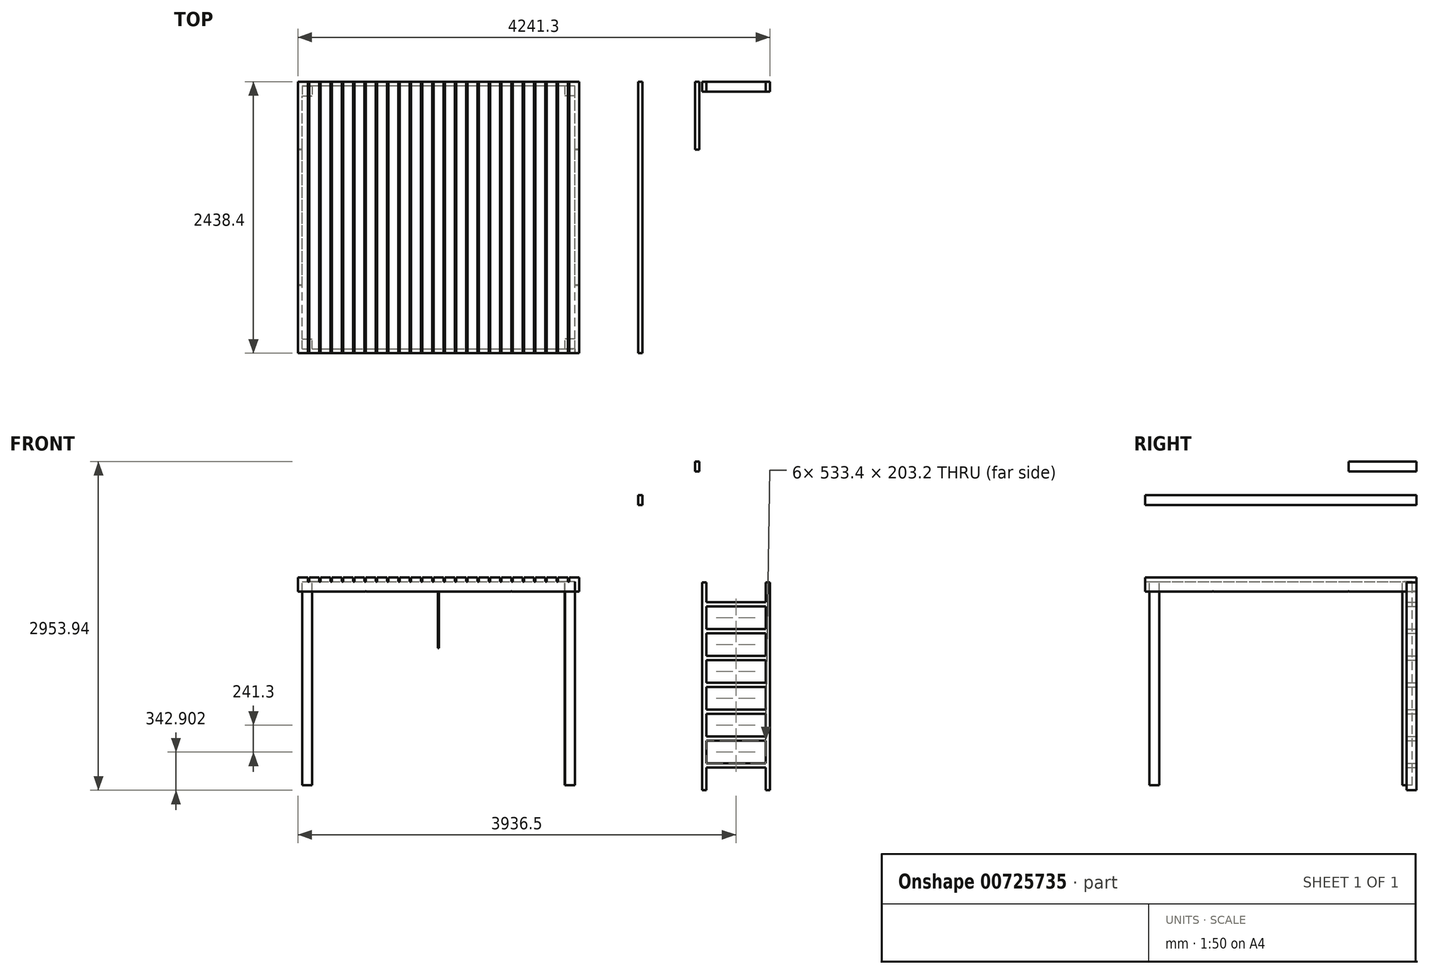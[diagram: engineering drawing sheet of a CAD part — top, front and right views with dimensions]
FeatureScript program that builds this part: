
annotation { "Feature Type Name" : "Feature", "Feature Type Description" : "" }
export const myFeature = defineFeature(function(context is Context, id is Id, definition is map)
    precondition{}
    {
        {
            var Q0;
            Q0=qCreatedBy(makeId("Front.planeOp"),FACE);
            var sketch = newSketch(context, id + "F0", { "sketchPlane" : qUnion([Q0])});
            skLineSegment(sketch, "E0.bottom", {"start": v(1225.55, 515.62) * mm, "end": v(-1225.55, 515.62) * mm});
            skLineSegment(sketch, "E0.top", {"start": v(1225.55, 604.52) * mm, "end": v(-1225.55, 604.52) * mm});
            skLineSegment(sketch, "E0.left", {"start": v(1225.55, 515.62) * mm, "end": v(1225.55, 604.52) * mm});
            skLineSegment(sketch, "E0.right", {"start": v(-1225.55, 515.62) * mm, "end": v(-1225.55, 604.52) * mm});
            skPoint(sketch, "E0.middle", {"position": v(0, 560.07) * mm});
            skLineSegment(sketch, "E1.bottom", {"start": v(1225.55, 515.62) * mm, "end": v(1263.65, 515.62) * mm});
            skLineSegment(sketch, "E1.top", {"start": v(1225.55, 604.52) * mm, "end": v(1263.65, 604.52) * mm});
            skLineSegment(sketch, "E1.right", {"start": v(1263.65, 515.62) * mm, "end": v(1263.65, 604.52) * mm});
            skLineSegment(sketch, "E2.bottom", {"start": v(-1225.55, 515.62) * mm, "end": v(-1263.65, 515.62) * mm});
            skLineSegment(sketch, "E2.top", {"start": v(-1225.55, 604.52) * mm, "end": v(-1263.65, 604.52) * mm});
            skLineSegment(sketch, "E2.right", {"start": v(-1263.65, 515.62) * mm, "end": v(-1263.65, 604.52) * mm});
            skLineSegment(sketch, "E3.bottom", {"start": v(-1263.65, 604.52) * mm, "end": v(-1174.75, 604.52) * mm});
            skLineSegment(sketch, "E3.top", {"start": v(-1263.65, 642.62) * mm, "end": v(-1174.75, 642.62) * mm});
            skLineSegment(sketch, "E3.left", {"start": v(-1263.65, 604.52) * mm, "end": v(-1263.65, 642.62) * mm});
            skLineSegment(sketch, "E3.right", {"start": v(-1174.75, 604.52) * mm, "end": v(-1174.75, 642.62) * mm});
            skLineSegment(sketch, "E4.bottom", {"start": v(-1162.05, 604.52) * mm, "end": v(-1073.15, 604.52) * mm});
            skLineSegment(sketch, "E4.top", {"start": v(-1162.05, 642.62) * mm, "end": v(-1073.15, 642.62) * mm});
            skLineSegment(sketch, "E4.left", {"start": v(-1162.05, 604.52) * mm, "end": v(-1162.05, 642.62) * mm});
            skLineSegment(sketch, "E4.right", {"start": v(-1073.15, 604.52) * mm, "end": v(-1073.15, 642.62) * mm});
            skLineSegment(sketch, "E5.bottom", {"start": v(-1060.45, 604.52) * mm, "end": v(-971.55, 604.52) * mm});
            skLineSegment(sketch, "E5.top", {"start": v(-1060.45, 642.62) * mm, "end": v(-971.55, 642.62) * mm});
            skLineSegment(sketch, "E5.left", {"start": v(-1060.45, 604.52) * mm, "end": v(-1060.45, 642.62) * mm});
            skLineSegment(sketch, "E5.right", {"start": v(-971.55, 604.52) * mm, "end": v(-971.55, 642.62) * mm});
            skLineSegment(sketch, "E6.bottom", {"start": v(-958.85, 604.52) * mm, "end": v(-869.95, 604.52) * mm});
            skLineSegment(sketch, "E6.top", {"start": v(-958.85, 642.62) * mm, "end": v(-869.95, 642.62) * mm});
            skLineSegment(sketch, "E6.left", {"start": v(-958.85, 604.52) * mm, "end": v(-958.85, 642.62) * mm});
            skLineSegment(sketch, "E6.right", {"start": v(-869.95, 604.52) * mm, "end": v(-869.95, 642.62) * mm});
            skLineSegment(sketch, "E7.bottom", {"start": v(-857.25, 604.52) * mm, "end": v(-768.35, 604.52) * mm});
            skLineSegment(sketch, "E7.top", {"start": v(-857.25, 642.62) * mm, "end": v(-768.35, 642.62) * mm});
            skLineSegment(sketch, "E7.left", {"start": v(-857.25, 604.52) * mm, "end": v(-857.25, 642.62) * mm});
            skLineSegment(sketch, "E7.right", {"start": v(-768.35, 604.52) * mm, "end": v(-768.35, 642.62) * mm});
            skLineSegment(sketch, "E8.bottom", {"start": v(-755.65, 604.52) * mm, "end": v(-666.75, 604.52) * mm});
            skLineSegment(sketch, "E8.top", {"start": v(-755.65, 642.62) * mm, "end": v(-666.75, 642.62) * mm});
            skLineSegment(sketch, "E8.left", {"start": v(-755.65, 604.52) * mm, "end": v(-755.65, 642.62) * mm});
            skLineSegment(sketch, "E8.right", {"start": v(-666.75, 604.52) * mm, "end": v(-666.75, 642.62) * mm});
            skLineSegment(sketch, "E9.bottom", {"start": v(-654.05, 604.52) * mm, "end": v(-565.15, 604.52) * mm});
            skLineSegment(sketch, "E9.top", {"start": v(-654.05, 642.62) * mm, "end": v(-565.15, 642.62) * mm});
            skLineSegment(sketch, "E9.left", {"start": v(-654.05, 604.52) * mm, "end": v(-654.05, 642.62) * mm});
            skLineSegment(sketch, "E9.right", {"start": v(-565.15, 604.52) * mm, "end": v(-565.15, 642.62) * mm});
            skLineSegment(sketch, "E10.bottom", {"start": v(-552.45, 604.52) * mm, "end": v(-463.55, 604.52) * mm});
            skLineSegment(sketch, "E10.top", {"start": v(-552.45, 642.62) * mm, "end": v(-463.55, 642.62) * mm});
            skLineSegment(sketch, "E10.left", {"start": v(-552.45, 604.52) * mm, "end": v(-552.45, 642.62) * mm});
            skLineSegment(sketch, "E10.right", {"start": v(-463.55, 604.52) * mm, "end": v(-463.55, 642.62) * mm});
            skLineSegment(sketch, "E11.bottom", {"start": v(-450.85, 604.52) * mm, "end": v(-361.95, 604.52) * mm});
            skLineSegment(sketch, "E11.top", {"start": v(-450.85, 642.62) * mm, "end": v(-361.95, 642.62) * mm});
            skLineSegment(sketch, "E11.left", {"start": v(-450.85, 604.52) * mm, "end": v(-450.85, 642.62) * mm});
            skLineSegment(sketch, "E11.right", {"start": v(-361.95, 604.52) * mm, "end": v(-361.95, 642.62) * mm});
            skLineSegment(sketch, "E12.bottom", {"start": v(-349.25, 604.52) * mm, "end": v(-260.35, 604.52) * mm});
            skLineSegment(sketch, "E12.top", {"start": v(-349.25, 642.62) * mm, "end": v(-260.35, 642.62) * mm});
            skLineSegment(sketch, "E12.left", {"start": v(-349.25, 604.52) * mm, "end": v(-349.25, 642.62) * mm});
            skLineSegment(sketch, "E12.right", {"start": v(-260.35, 604.52) * mm, "end": v(-260.35, 642.62) * mm});
            skLineSegment(sketch, "E13.bottom", {"start": v(-247.65, 604.52) * mm, "end": v(-158.75, 604.52) * mm});
            skLineSegment(sketch, "E13.top", {"start": v(-247.65, 642.62) * mm, "end": v(-158.75, 642.62) * mm});
            skLineSegment(sketch, "E13.left", {"start": v(-247.65, 604.52) * mm, "end": v(-247.65, 642.62) * mm});
            skLineSegment(sketch, "E13.right", {"start": v(-158.75, 604.52) * mm, "end": v(-158.75, 642.62) * mm});
            skLineSegment(sketch, "E14.bottom", {"start": v(-146.05, 604.52) * mm, "end": v(-57.15, 604.52) * mm});
            skLineSegment(sketch, "E14.top", {"start": v(-146.05, 642.62) * mm, "end": v(-57.15, 642.62) * mm});
            skLineSegment(sketch, "E14.left", {"start": v(-146.05, 604.52) * mm, "end": v(-146.05, 642.62) * mm});
            skLineSegment(sketch, "E14.right", {"start": v(-57.15, 604.52) * mm, "end": v(-57.15, 642.62) * mm});
            skLineSegment(sketch, "E15.MirrorCS", {"start": v(57.15, 604.52) * mm, "end": v(57.15, 642.62) * mm});
            skLineSegment(sketch, "E16.MirrorCS", {"start": v(146.05, 642.62) * mm, "end": v(57.15, 642.62) * mm});
            skLineSegment(sketch, "E17.MirrorCS", {"start": v(146.05, 604.52) * mm, "end": v(146.05, 642.62) * mm});
            skLineSegment(sketch, "E18.MirrorCS", {"start": v(158.75, 604.52) * mm, "end": v(158.75, 642.62) * mm});
            skLineSegment(sketch, "E19.MirrorCS", {"start": v(247.65, 642.62) * mm, "end": v(158.75, 642.62) * mm});
            skLineSegment(sketch, "E20.MirrorCS", {"start": v(247.65, 604.52) * mm, "end": v(247.65, 642.62) * mm});
            skLineSegment(sketch, "E21.MirrorCS", {"start": v(260.35, 604.52) * mm, "end": v(260.35, 642.62) * mm});
            skLineSegment(sketch, "E22.MirrorCS", {"start": v(349.25, 642.62) * mm, "end": v(260.35, 642.62) * mm});
            skLineSegment(sketch, "E23.MirrorCS", {"start": v(349.25, 604.52) * mm, "end": v(349.25, 642.62) * mm});
            skLineSegment(sketch, "E24.MirrorCS", {"start": v(361.95, 604.52) * mm, "end": v(361.95, 642.62) * mm});
            skLineSegment(sketch, "E25.MirrorCS", {"start": v(450.85, 642.62) * mm, "end": v(361.95, 642.62) * mm});
            skLineSegment(sketch, "E26.MirrorCS", {"start": v(450.85, 604.52) * mm, "end": v(450.85, 642.62) * mm});
            skLineSegment(sketch, "E27.MirrorCS", {"start": v(463.55, 604.52) * mm, "end": v(463.55, 642.62) * mm});
            skLineSegment(sketch, "E28.MirrorCS", {"start": v(552.45, 642.62) * mm, "end": v(463.55, 642.62) * mm});
            skLineSegment(sketch, "E29.MirrorCS", {"start": v(552.45, 604.52) * mm, "end": v(552.45, 642.62) * mm});
            skLineSegment(sketch, "E30.MirrorCS", {"start": v(565.15, 604.52) * mm, "end": v(565.15, 642.62) * mm});
            skLineSegment(sketch, "E31.MirrorCS", {"start": v(654.05, 642.62) * mm, "end": v(565.15, 642.62) * mm});
            skLineSegment(sketch, "E32.MirrorCS", {"start": v(654.05, 604.52) * mm, "end": v(654.05, 642.62) * mm});
            skLineSegment(sketch, "E33.MirrorCS", {"start": v(666.75, 604.52) * mm, "end": v(666.75, 642.62) * mm});
            skLineSegment(sketch, "E34.MirrorCS", {"start": v(755.65, 642.62) * mm, "end": v(666.75, 642.62) * mm});
            skLineSegment(sketch, "E35.MirrorCS", {"start": v(755.65, 604.52) * mm, "end": v(755.65, 642.62) * mm});
            skLineSegment(sketch, "E36.MirrorCS", {"start": v(768.35, 604.52) * mm, "end": v(768.35, 642.62) * mm});
            skLineSegment(sketch, "E37.MirrorCS", {"start": v(857.25, 642.62) * mm, "end": v(768.35, 642.62) * mm});
            skLineSegment(sketch, "E38.MirrorCS", {"start": v(857.25, 604.52) * mm, "end": v(857.25, 642.62) * mm});
            skLineSegment(sketch, "E39.MirrorCS", {"start": v(869.95, 604.52) * mm, "end": v(869.95, 642.62) * mm});
            skLineSegment(sketch, "E40.MirrorCS", {"start": v(958.85, 642.62) * mm, "end": v(869.95, 642.62) * mm});
            skLineSegment(sketch, "E41.MirrorCS", {"start": v(1263.65, 604.52) * mm, "end": v(1263.65, 642.62) * mm});
            skLineSegment(sketch, "E42.MirrorCS", {"start": v(1263.65, 642.62) * mm, "end": v(1174.75, 642.62) * mm});
            skLineSegment(sketch, "E43.MirrorCS", {"start": v(1174.75, 604.52) * mm, "end": v(1174.75, 642.62) * mm});
            skLineSegment(sketch, "E44.MirrorCS", {"start": v(1162.05, 604.52) * mm, "end": v(1162.05, 642.62) * mm});
            skLineSegment(sketch, "E45.MirrorCS", {"start": v(1162.05, 642.62) * mm, "end": v(1073.15, 642.62) * mm});
            skLineSegment(sketch, "E46.MirrorCS", {"start": v(1073.15, 604.52) * mm, "end": v(1073.15, 642.62) * mm});
            skLineSegment(sketch, "E47.MirrorCS", {"start": v(1060.45, 604.52) * mm, "end": v(1060.45, 642.62) * mm});
            skLineSegment(sketch, "E48.MirrorCS", {"start": v(1060.45, 642.62) * mm, "end": v(971.55, 642.62) * mm});
            skLineSegment(sketch, "E49.MirrorCS", {"start": v(971.55, 604.52) * mm, "end": v(971.55, 642.62) * mm});
            skLineSegment(sketch, "E50.MirrorCS", {"start": v(958.85, 604.52) * mm, "end": v(958.85, 642.62) * mm});
            skLineSegment(sketch, "E51.bottom", {"start": v(-44.45, 604.52) * mm, "end": v(44.45, 604.52) * mm});
            skLineSegment(sketch, "E51.top", {"start": v(-44.45, 642.62) * mm, "end": v(44.45, 642.62) * mm});
            skLineSegment(sketch, "E51.left", {"start": v(-44.45, 604.52) * mm, "end": v(-44.45, 642.62) * mm});
            skLineSegment(sketch, "E51.right", {"start": v(44.45, 604.52) * mm, "end": v(44.45, 642.62) * mm});
            skLineSegment(sketch, "E52.bottom", {"start": v(4.76, 7.62) * mm, "end": v(-4.76, 7.62) * mm});
            skLineSegment(sketch, "E52.top", {"start": v(4.76, 515.62) * mm, "end": v(-4.76, 515.62) * mm});
            skLineSegment(sketch, "E52.left", {"start": v(4.76, 7.62) * mm, "end": v(4.76, 515.62) * mm});
            skLineSegment(sketch, "E52.right", {"start": v(-4.76, 7.62) * mm, "end": v(-4.76, 515.62) * mm});
            skPoint(sketch, "E52.middle", {"position": v(0, 261.62) * mm});
            skLineSegment(sketch, "E53.bottom", {"start": v(2977.65, -1270.8) * mm, "end": v(2939.55, -1270.8) * mm});
            skLineSegment(sketch, "E53.top", {"start": v(2977.65, 596.1) * mm, "end": v(2939.55, 596.1) * mm});
            skLineSegment(sketch, "E53.left", {"start": v(2977.65, -1270.8) * mm, "end": v(2977.65, 596.1) * mm});
            skLineSegment(sketch, "E53.right", {"start": v(2368.05, -1270.8) * mm, "end": v(2368.05, 596.1) * mm});
            skPoint(sketch, "E53.middle", {"position": v(2672.85, -337.35) * mm});
            skLineSegment(sketch, "E54.left", {"start": v(2939.55, -1270.8) * mm, "end": v(2939.55, -1067.6) * mm});
            skLineSegment(sketch, "E54.right", {"start": v(2406.15, -1270.8) * mm, "end": v(2406.15, -1067.6) * mm});
            skLineSegment(sketch, "E55", {"start": v(2406.15, -1067.6) * mm, "end": v(2939.55, -1067.6) * mm});
            skLineSegment(sketch, "E56", {"start": v(2406.15, -1029.5) * mm, "end": v(2939.55, -1029.5) * mm});
            skLineSegment(sketch, "E57", {"start": v(2406.15, -826.3) * mm, "end": v(2939.55, -826.3) * mm});
            skPoint(sketch, "E58.orphan", {"position": v(2939.55, -337.35) * mm});
            skPoint(sketch, "E59.start.orphan", {"position": v(2406.15, -337.35) * mm});
            skLineSegment(sketch, "E60", {"start": v(2406.15, -788.2) * mm, "end": v(2939.55, -788.2) * mm});
            skLineSegment(sketch, "E61", {"start": v(2406.15, -585) * mm, "end": v(2939.55, -585) * mm});
            skLineSegment(sketch, "E62", {"start": v(2406.15, -546.9) * mm, "end": v(2939.55, -546.9) * mm});
            skLineSegment(sketch, "E63", {"start": v(2939.55, -343.7) * mm, "end": v(2406.15, -343.7) * mm});
            skLineSegment(sketch, "E64", {"start": v(2406.15, -305.6) * mm, "end": v(2939.55, -305.6) * mm});
            skLineSegment(sketch, "E65", {"start": v(2406.15, -102.4) * mm, "end": v(2939.55, -102.4) * mm});
            skLineSegment(sketch, "E66", {"start": v(2406.15, -64.3) * mm, "end": v(2939.55, -64.3) * mm});
            skLineSegment(sketch, "E67", {"start": v(2406.15, 138.9) * mm, "end": v(2939.55, 138.9) * mm});
            skLineSegment(sketch, "E68", {"start": v(2406.15, 177) * mm, "end": v(2939.55, 177) * mm});
            skLineSegment(sketch, "E69", {"start": v(2406.15, 380.2) * mm, "end": v(2939.55, 380.2) * mm});
            skLineSegment(sketch, "E70", {"start": v(2406.15, 418.3) * mm, "end": v(2939.55, 418.3) * mm});
            skLineSegment(sketch, "E71.trimOffspring", {"start": v(2406.15, 596.1) * mm, "end": v(2368.05, 596.1) * mm});
            skLineSegment(sketch, "E72.trimOffspring", {"start": v(2406.15, -1270.8) * mm, "end": v(2368.05, -1270.8) * mm});
            skLineSegment(sketch, "E73.trimOffspring", {"start": v(2939.55, -1029.5) * mm, "end": v(2939.55, -826.3) * mm});
            skLineSegment(sketch, "E74.trimOffspring", {"start": v(2939.55, -788.2) * mm, "end": v(2939.55, -585) * mm});
            skLineSegment(sketch, "E75.trimOffspring", {"start": v(2406.15, -1029.5) * mm, "end": v(2406.15, -826.3) * mm});
            skLineSegment(sketch, "E76.trimOffspring", {"start": v(2406.15, -788.2) * mm, "end": v(2406.15, -585) * mm});
            skLineSegment(sketch, "E77.trimOffspring", {"start": v(2406.15, -546.9) * mm, "end": v(2406.15, -343.7) * mm});
            skLineSegment(sketch, "E78.trimOffspring", {"start": v(2939.55, -546.9) * mm, "end": v(2939.55, -343.7) * mm});
            skLineSegment(sketch, "E79.trimOffspring", {"start": v(2939.55, -305.6) * mm, "end": v(2939.55, -102.4) * mm});
            skLineSegment(sketch, "E80.trimOffspring", {"start": v(2406.15, -305.6) * mm, "end": v(2406.15, -102.4) * mm});
            skLineSegment(sketch, "E81.trimOffspring", {"start": v(2406.15, -64.3) * mm, "end": v(2406.15, 138.9) * mm});
            skLineSegment(sketch, "E82.trimOffspring", {"start": v(2939.55, -64.3) * mm, "end": v(2939.55, 138.9) * mm});
            skLineSegment(sketch, "E83.trimOffspring", {"start": v(2406.15, 177) * mm, "end": v(2406.15, 380.2) * mm});
            skLineSegment(sketch, "E84.trimOffspring", {"start": v(2939.55, 177) * mm, "end": v(2939.55, 380.2) * mm});
            skLineSegment(sketch, "E85.trimOffspring", {"start": v(2406.15, 418.3) * mm, "end": v(2406.15, 596.1) * mm});
            skLineSegment(sketch, "E86.trimOffspring", {"start": v(2939.55, 418.3) * mm, "end": v(2939.55, 596.1) * mm});
            skLineSegment(sketch, "E87.bottom", {"start": v(1833.2, 1291.68) * mm, "end": v(1795.1, 1291.68) * mm});
            skLineSegment(sketch, "E87.top", {"start": v(1833.2, 1380.58) * mm, "end": v(1795.1, 1380.58) * mm});
            skLineSegment(sketch, "E87.left", {"start": v(1833.2, 1291.68) * mm, "end": v(1833.2, 1380.58) * mm});
            skLineSegment(sketch, "E87.right", {"start": v(1795.1, 1291.68) * mm, "end": v(1795.1, 1380.58) * mm});
            skPoint(sketch, "E87.middle", {"position": v(1814.15, 1336.13) * mm});
            skLineSegment(sketch, "E88.bottom", {"start": v(2342.66, 1594.24) * mm, "end": v(2304.56, 1594.24) * mm});
            skLineSegment(sketch, "E88.top", {"start": v(2342.66, 1683.14) * mm, "end": v(2304.56, 1683.14) * mm});
            skLineSegment(sketch, "E88.left", {"start": v(2342.66, 1594.24) * mm, "end": v(2342.66, 1683.14) * mm});
            skLineSegment(sketch, "E88.right", {"start": v(2304.56, 1594.24) * mm, "end": v(2304.56, 1683.14) * mm});
            skPoint(sketch, "E88.middle", {"position": v(2323.6, 1638.69) * mm});
            skPoint(sketch, "E89", {"position": v(530.16, 1053.68) * mm});
            skPoint(sketch, "E90", {"position": v(654.05, 515.62) * mm});
            skPoint(sketch, "E91", {"position": v(-654.05, 515.62) * mm});
            skSolve(sketch);
        }
        {
            var Q0;
            Q0=makeQuery(id+"F0.imprint","IMPRINT",FACE,{"disambiguationData":[TD([[makeQuery(id+"F0.imprint","IMPRINT",EDGE,{"derivedFrom":sQuery(id+"F0.wireOp",EDGE,"E0.left")}),-1.0]])]});
            var Q1;
            Q1=makeQuery(id+"F0.imprint","IMPRINT",FACE,{"disambiguationData":[TD([[makeQuery(id+"F0.imprint","IMPRINT",EDGE,{"derivedFrom":sQuery(id+"F0.wireOp",EDGE,"E0.right")}),1.0]])]});
            extrude(context, id + "F1", {"entities" : qUnion([Q0, Q1]), "depth" : 2438.4 * mm, "offsetDistance" : 25.4 * mm});
        }
        {
            var Q0;
            {var subQ37=sQuery(id+"F0.wireOp",EDGE,"E0.left");Q0=makeQuery(id+"F0.imprint","IMPRINT",FACE,{"disambiguationData":[TD([[makeQuery(id+"F0.imprint","IMPRINT",EDGE,{"derivedFrom":subQ37}),1.0]])]});}
            extrude(context, id + "F2", {"entities" : qUnion([Q0]), "operationType" : NewBodyOperationType.ADD, "depth" : 38.1 * mm, "offsetDistance" : 25.4 * mm});
        }
        {
            var Q0;
            Q0=makeQuery(id+"F2.boolean.opBoolean","MERGE",FACE,{"derivedFrom":[makeQuery(id+"F1.opExtrude","SWEPT_FACE",FACE,{"disambiguationData":[OSD([sQuery(id+"F0.wireOp",EDGE,"E1.top")])]}),makeQuery(id+"F1.opExtrude","SWEPT_FACE",FACE,{"disambiguationData":[OSD([sQuery(id+"F0.wireOp",EDGE,"E2.top")])]}),makeQuery(id+"F2.opExtrude","SWEPT_FACE",FACE,{"disambiguationData":[OSD([sQuery(id+"F0.wireOp",EDGE,"E0.top")])]})]});
            cPlane(context, id + "F3", {"entities" : qUnion([Q0]), "cplaneType" : CPlaneType.OFFSET, "offset" : 0 * mm, "width" : 152.4 * mm, "height" : 152.4 * mm});
        }
        {
            var Q0;
            Q0=qCreatedBy(id+"F3.planeOp",FACE);
            var sketch = newSketch(context, id + "F4", { "sketchPlane" : qUnion([Q0])});
            skLineSegment(sketch, "E92.bottom", {"start": v(-1225.55, -2400.3) * mm, "end": v(-1136.65, -2400.3) * mm});
            skLineSegment(sketch, "E92.top", {"start": v(-1225.55, -2311.4) * mm, "end": v(-1136.65, -2311.4) * mm});
            skLineSegment(sketch, "E92.left", {"start": v(-1225.55, -2400.3) * mm, "end": v(-1225.55, -2311.4) * mm});
            skLineSegment(sketch, "E92.right", {"start": v(-1136.65, -2400.3) * mm, "end": v(-1136.65, -2311.4) * mm});
            skLineSegment(sketch, "E93.bottom", {"start": v(1225.55, -2400.3) * mm, "end": v(1136.65, -2400.3) * mm});
            skLineSegment(sketch, "E93.top", {"start": v(1225.55, -2311.4) * mm, "end": v(1136.65, -2311.4) * mm});
            skLineSegment(sketch, "E93.left", {"start": v(1225.55, -2400.3) * mm, "end": v(1225.55, -2311.4) * mm});
            skLineSegment(sketch, "E93.right", {"start": v(1136.65, -2400.3) * mm, "end": v(1136.65, -2311.4) * mm});
            skLineSegment(sketch, "E94.bottom", {"start": v(-1226.27, -2400.3) * mm, "end": v(1224.83, -2400.3) * mm});
            skLineSegment(sketch, "E94.top", {"start": v(-1226.27, -2438.4) * mm, "end": v(1224.83, -2438.4) * mm});
            skLineSegment(sketch, "E94.left", {"start": v(-1226.27, -2400.3) * mm, "end": v(-1226.27, -2438.4) * mm});
            skLineSegment(sketch, "E94.right", {"start": v(1224.83, -2400.3) * mm, "end": v(1224.83, -2438.4) * mm});
            skLineSegment(sketch, "E95.bottom", {"start": v(-1226.02, -38.43) * mm, "end": v(-1137.12, -38.43) * mm});
            skLineSegment(sketch, "E95.top", {"start": v(-1226.02, -127.33) * mm, "end": v(-1137.12, -127.33) * mm});
            skLineSegment(sketch, "E95.left", {"start": v(-1226.02, -38.43) * mm, "end": v(-1226.02, -127.33) * mm});
            skLineSegment(sketch, "E95.right", {"start": v(-1137.12, -38.43) * mm, "end": v(-1137.12, -127.33) * mm});
            skLineSegment(sketch, "E96.bottom", {"start": v(1223.57, -39.1) * mm, "end": v(1134.67, -39.1) * mm});
            skLineSegment(sketch, "E96.top", {"start": v(1223.57, -128) * mm, "end": v(1134.67, -128) * mm});
            skLineSegment(sketch, "E96.left", {"start": v(1223.57, -39.1) * mm, "end": v(1223.57, -128) * mm});
            skLineSegment(sketch, "E96.right", {"start": v(1134.67, -39.1) * mm, "end": v(1134.67, -128) * mm});
            skSolve(sketch);
        }
        {
            var Q0;
            {var subQ1=sQuery(id+"F4.wireOp",EDGE,"E92.bottom");Q0=makeQuery(id+"F4.imprint","IMPRINT",FACE,{"disambiguationData":[TD([[makeQuery(id+"F4.imprint","IMPRINT",EDGE,{"derivedFrom":subQ1}),-1.0]])]});}
            extrude(context, id + "F5", {"entities" : qUnion([Q0]), "operationType" : NewBodyOperationType.ADD, "oppositeDirection" : true, "depth" : 88.9 * mm, "offsetDistance" : 25.4 * mm});
        }
        {
            var Q0;
            Q0=makeQuery(id+"F4.imprint","IMPRINT",FACE,{"disambiguationData":[TD([[makeQuery(id+"F4.imprint","IMPRINT",EDGE,{"derivedFrom":sQuery(id+"F4.wireOp",EDGE,"E92.bottom")}),1.0]])]});
            extrude(context, id + "F6", {"entities" : qUnion([Q0]), "operationType" : NewBodyOperationType.ADD, "oppositeDirection" : true, "depth" : 1828.8 * mm, "offsetDistance" : 25.4 * mm});
        }
        {
            var Q0;
            Q0=makeQuery(id+"F4.imprint","IMPRINT",FACE,{"disambiguationData":[TD([[makeQuery(id+"F4.imprint","IMPRINT",EDGE,{"derivedFrom":sQuery(id+"F4.wireOp",EDGE,"E93.top")}),1.0]])]});
            extrude(context, id + "F7", {"entities" : qUnion([Q0]), "operationType" : NewBodyOperationType.ADD, "oppositeDirection" : true, "depth" : 1828.8 * mm, "offsetDistance" : 25.4 * mm});
        }
        {
            var Q0;
            Q0=makeQuery(id+"F0.imprint","IMPRINT",FACE,{"disambiguationData":[TD([[makeQuery(id+"F0.imprint","IMPRINT",EDGE,{"derivedFrom":sQuery(id+"F0.wireOp",EDGE,"E52.bottom")}),-1.0]])]});
            extrude(context, id + "F8", {"entities" : qUnion([Q0]), "operationType" : NewBodyOperationType.ADD, "depth" : 3.17 * mm, "offsetDistance" : 25.4 * mm});
        }
        {
            var Q0;
            {var subQ0=sQuery(id+"F0.wireOp",EDGE,"E18.MirrorCS");Q0=makeQuery(id+"F0.imprint","IMPRINT",FACE,{"disambiguationData":[TD([[makeQuery(id+"F0.imprint","IMPRINT",EDGE,{"derivedFrom":subQ0}),-1.0]])]});}
            var Q1;
            {var subQ0=sQuery(id+"F0.wireOp",EDGE,"E15.MirrorCS");Q1=makeQuery(id+"F0.imprint","IMPRINT",FACE,{"disambiguationData":[TD([[makeQuery(id+"F0.imprint","IMPRINT",EDGE,{"derivedFrom":subQ0}),-1.0]])]});}
            var Q2;
            Q2=makeQuery(id+"F0.imprint","IMPRINT",FACE,{"disambiguationData":[TD([[makeQuery(id+"F0.imprint","IMPRINT",EDGE,{"derivedFrom":sQuery(id+"F0.wireOp",EDGE,"E11.top")}),-1.0]])]});
            var Q3;
            Q3=makeQuery(id+"F0.imprint","IMPRINT",FACE,{"disambiguationData":[TD([[makeQuery(id+"F0.imprint","IMPRINT",EDGE,{"derivedFrom":sQuery(id+"F0.wireOp",EDGE,"E4.top")}),-1.0]])]});
            var Q4;
            Q4=makeQuery(id+"F0.imprint","IMPRINT",FACE,{"disambiguationData":[TD([[makeQuery(id+"F0.imprint","IMPRINT",EDGE,{"derivedFrom":sQuery(id+"F0.wireOp",EDGE,"E6.top")}),-1.0]])]});
            var Q5;
            {var subQ0=sQuery(id+"F0.wireOp",EDGE,"E44.MirrorCS");Q5=makeQuery(id+"F0.imprint","IMPRINT",FACE,{"disambiguationData":[TD([[makeQuery(id+"F0.imprint","IMPRINT",EDGE,{"derivedFrom":subQ0}),1.0]])]});}
            var Q6;
            Q6=makeQuery(id+"F0.imprint","IMPRINT",FACE,{"disambiguationData":[TD([[makeQuery(id+"F0.imprint","IMPRINT",EDGE,{"derivedFrom":sQuery(id+"F0.wireOp",EDGE,"E5.top")}),-1.0]])]});
            var Q7;
            {var subQ0=sQuery(id+"F0.wireOp",EDGE,"E21.MirrorCS");Q7=makeQuery(id+"F0.imprint","IMPRINT",FACE,{"disambiguationData":[TD([[makeQuery(id+"F0.imprint","IMPRINT",EDGE,{"derivedFrom":subQ0}),-1.0]])]});}
            var Q8;
            Q8=makeQuery(id+"F0.imprint","IMPRINT",FACE,{"disambiguationData":[TD([[makeQuery(id+"F0.imprint","IMPRINT",EDGE,{"derivedFrom":sQuery(id+"F0.wireOp",EDGE,"E9.top")}),-1.0]])]});
            var Q9;
            {var subQ0=sQuery(id+"F0.wireOp",EDGE,"E2.top");Q9=makeQuery(id+"F0.imprint","IMPRINT",FACE,{"disambiguationData":[TD([[makeQuery(id+"F0.imprint","IMPRINT",EDGE,{"derivedFrom":subQ0}),-1.0]])]});}
            var Q10;
            {var subQ0=sQuery(id+"F0.wireOp",EDGE,"E30.MirrorCS");Q10=makeQuery(id+"F0.imprint","IMPRINT",FACE,{"disambiguationData":[TD([[makeQuery(id+"F0.imprint","IMPRINT",EDGE,{"derivedFrom":subQ0}),-1.0]])]});}
            var Q11;
            Q11=makeQuery(id+"F0.imprint","IMPRINT",FACE,{"disambiguationData":[TD([[makeQuery(id+"F0.imprint","IMPRINT",EDGE,{"derivedFrom":sQuery(id+"F0.wireOp",EDGE,"E10.top")}),-1.0]])]});
            var Q12;
            {var subQ0=sQuery(id+"F0.wireOp",EDGE,"E24.MirrorCS");Q12=makeQuery(id+"F0.imprint","IMPRINT",FACE,{"disambiguationData":[TD([[makeQuery(id+"F0.imprint","IMPRINT",EDGE,{"derivedFrom":subQ0}),-1.0]])]});}
            var Q13;
            {var subQ0=sQuery(id+"F0.wireOp",EDGE,"E27.MirrorCS");Q13=makeQuery(id+"F0.imprint","IMPRINT",FACE,{"disambiguationData":[TD([[makeQuery(id+"F0.imprint","IMPRINT",EDGE,{"derivedFrom":subQ0}),-1.0]])]});}
            var Q14;
            Q14=makeQuery(id+"F0.imprint","IMPRINT",FACE,{"disambiguationData":[TD([[makeQuery(id+"F0.imprint","IMPRINT",EDGE,{"derivedFrom":sQuery(id+"F0.wireOp",EDGE,"E13.top")}),-1.0]])]});
            var Q15;
            {var subQ0=sQuery(id+"F0.wireOp",EDGE,"E39.MirrorCS");Q15=makeQuery(id+"F0.imprint","IMPRINT",FACE,{"disambiguationData":[TD([[makeQuery(id+"F0.imprint","IMPRINT",EDGE,{"derivedFrom":subQ0}),-1.0]])]});}
            var Q16;
            Q16=makeQuery(id+"F0.imprint","IMPRINT",FACE,{"disambiguationData":[TD([[makeQuery(id+"F0.imprint","IMPRINT",EDGE,{"derivedFrom":sQuery(id+"F0.wireOp",EDGE,"E7.top")}),-1.0]])]});
            var Q17;
            {var subQ0=sQuery(id+"F0.wireOp",EDGE,"E33.MirrorCS");Q17=makeQuery(id+"F0.imprint","IMPRINT",FACE,{"disambiguationData":[TD([[makeQuery(id+"F0.imprint","IMPRINT",EDGE,{"derivedFrom":subQ0}),-1.0]])]});}
            var Q18;
            {var subQ0=sQuery(id+"F0.wireOp",EDGE,"E36.MirrorCS");Q18=makeQuery(id+"F0.imprint","IMPRINT",FACE,{"disambiguationData":[TD([[makeQuery(id+"F0.imprint","IMPRINT",EDGE,{"derivedFrom":subQ0}),-1.0]])]});}
            var Q19;
            {var subQ0=sQuery(id+"F0.wireOp",EDGE,"E47.MirrorCS");Q19=makeQuery(id+"F0.imprint","IMPRINT",FACE,{"disambiguationData":[TD([[makeQuery(id+"F0.imprint","IMPRINT",EDGE,{"derivedFrom":subQ0}),1.0]])]});}
            var Q20;
            Q20=makeQuery(id+"F0.imprint","IMPRINT",FACE,{"disambiguationData":[TD([[makeQuery(id+"F0.imprint","IMPRINT",EDGE,{"derivedFrom":sQuery(id+"F0.wireOp",EDGE,"E8.top")}),-1.0]])]});
            var Q21;
            {var subQ0=sQuery(id+"F0.wireOp",EDGE,"E1.top");Q21=makeQuery(id+"F0.imprint","IMPRINT",FACE,{"disambiguationData":[TD([[makeQuery(id+"F0.imprint","IMPRINT",EDGE,{"derivedFrom":subQ0}),1.0]])]});}
            var Q22;
            Q22=makeQuery(id+"F0.imprint","IMPRINT",FACE,{"disambiguationData":[TD([[makeQuery(id+"F0.imprint","IMPRINT",EDGE,{"derivedFrom":sQuery(id+"F0.wireOp",EDGE,"E51.top")}),-1.0]])]});
            var Q23;
            Q23=makeQuery(id+"F0.imprint","IMPRINT",FACE,{"disambiguationData":[TD([[makeQuery(id+"F0.imprint","IMPRINT",EDGE,{"derivedFrom":sQuery(id+"F0.wireOp",EDGE,"E12.top")}),-1.0]])]});
            var Q24;
            Q24=makeQuery(id+"F0.imprint","IMPRINT",FACE,{"disambiguationData":[TD([[makeQuery(id+"F0.imprint","IMPRINT",EDGE,{"derivedFrom":sQuery(id+"F0.wireOp",EDGE,"E14.top")}),-1.0]])]});
            extrude(context, id + "F9", {"entities" : qUnion([Q0, Q1, Q2, Q3, Q4, Q5, Q6, Q7, Q8, Q9, Q10, Q11, Q12, Q13, Q14, Q15, Q16, Q17, Q18, Q19, Q20, Q21, Q22, Q23, Q24]), "operationType" : NewBodyOperationType.ADD, "depth" : 2438.4 * mm, "offsetDistance" : 25.4 * mm});
        }
        {
            var Q0;
            Q0=makeQuery(id+"F0.imprint","IMPRINT",FACE,{"disambiguationData":[TD([[makeQuery(id+"F0.imprint","IMPRINT",EDGE,{"derivedFrom":sQuery(id+"F0.wireOp",EDGE,"E53.bottom")}),-1.0]])]});
            extrude(context, id + "F10", {"entities" : qUnion([Q0]), "depth" : 88.9 * mm, "offsetDistance" : 25.4 * mm});
        }
        {
            var Q0;
            Q0=makeQuery(id+"F4.imprint","IMPRINT",FACE,{"disambiguationData":[TD([[makeQuery(id+"F4.imprint","IMPRINT",EDGE,{"derivedFrom":sQuery(id+"F4.wireOp",EDGE,"E95.bottom")}),-1.0]])]});
            var Q1;
            Q1=makeQuery(id+"F4.imprint","IMPRINT",FACE,{"disambiguationData":[TD([[makeQuery(id+"F4.imprint","IMPRINT",EDGE,{"derivedFrom":sQuery(id+"F4.wireOp",EDGE,"E96.bottom")}),1.0]])]});
            extrude(context, id + "F11", {"entities" : qUnion([Q0, Q1]), "operationType" : NewBodyOperationType.ADD, "oppositeDirection" : true, "depth" : 1828.8 * mm, "offsetDistance" : 25.4 * mm});
        }
        {
            var Q0;
            Q0=makeQuery(id+"F0.imprint","IMPRINT",FACE,{"disambiguationData":[TD([[makeQuery(id+"F0.imprint","IMPRINT",EDGE,{"derivedFrom":sQuery(id+"F0.wireOp",EDGE,"E88.bottom")}),-1.0]])]});
            extrude(context, id + "F12", {"entities" : qUnion([Q0]), "depth" : 609.6 * mm, "offsetDistance" : 25.4 * mm});
        }
        {
            var Q0;
            Q0=makeQuery(id+"F0.imprint","IMPRINT",FACE,{"disambiguationData":[TD([[makeQuery(id+"F0.imprint","IMPRINT",EDGE,{"derivedFrom":sQuery(id+"F0.wireOp",EDGE,"E87.bottom")}),-1.0]])]});
            extrude(context, id + "F13", {"entities" : qUnion([Q0]), "depth" : 2438.4 * mm, "offsetDistance" : 25.4 * mm});
        }
        {
            var Q0;
            Q0=makeQuery(id+"F9.boolean.opBoolean","MERGE",FACE,{"derivedFrom":[makeQuery(id+"F1.opExtrude","SWEPT_FACE",FACE,{"disambiguationData":[OSD([sQuery(id+"F0.wireOp",EDGE,"E1.right")])]}),makeQuery(id+"F9.opExtrude","SWEPT_FACE",FACE,{"disambiguationData":[OSD([sQuery(id+"F0.wireOp",EDGE,"E41.MirrorCS")])]})]});
            cPlane(context, id + "F14", {"entities" : qUnion([Q0]), "cplaneType" : CPlaneType.OFFSET, "offset" : 25.4 * mm, "width" : 152.4 * mm, "height" : 152.4 * mm});
        }
        {
            var Q0;
            Q0=qCreatedBy(id+"F14.planeOp",FACE);
            var sketch = newSketch(context, id + "F15", { "sketchPlane" : qUnion([Q0])});
            skPoint(sketch, "E97", {"position": v(-609.6, 641.02) * mm});
            skPoint(sketch, "E98", {"position": v(-1828.8, 640.67) * mm});
            skPoint(sketch, "E99", {"position": v(-609.6, 515.62) * mm});
            skPoint(sketch, "E100", {"position": v(-1828.8, 515.62) * mm});
            skSolve(sketch);
        }
        {
            var Q0;
            Q0=sQuery(id+"F15.wireOp",VERTEX,"E100");
            var Q1;
            Q1=makeQuery(id+"F1.opExtrude","SWEPT_BODY",BODY,{"disambiguationData":[OSD([sQuery(id+"F0.wireOp",EDGE,"E0.left"),sQuery(id+"F0.wireOp",EDGE,"E1.bottom"),sQuery(id+"F0.wireOp",EDGE,"E1.top"),sQuery(id+"F0.wireOp",EDGE,"E1.right")])]});
            hole(context, id + "F16", {"style" : HoleStyle.SIMPLE, "endStyle" : HoleEndStyle.THROUGH, "holeDiameter" : 6.35 * mm, "majorDiameter" : 6.35 * mm, "isTappedThrough" : true, "tappedDepth" : 12.7 * mm, "tapClearance" : 3, "locations" : qUnion([Q0]), "scope" : qUnion([Q1])});
        }
        {
            var Q0;
            Q0=sQuery(id+"F15.wireOp",VERTEX,"E99");
            var Q1;
            Q1=makeQuery(id+"F1.opExtrude","SWEPT_BODY",BODY,{"disambiguationData":[OSD([sQuery(id+"F0.wireOp",EDGE,"E0.left"),sQuery(id+"F0.wireOp",EDGE,"E1.bottom"),sQuery(id+"F0.wireOp",EDGE,"E1.top"),sQuery(id+"F0.wireOp",EDGE,"E1.right")])]});
            hole(context, id + "F17", {"style" : HoleStyle.SIMPLE, "endStyle" : HoleEndStyle.THROUGH, "holeDiameter" : 6.35 * mm, "majorDiameter" : 6.35 * mm, "isTappedThrough" : true, "tappedDepth" : 12.7 * mm, "tapClearance" : 3, "locations" : qUnion([Q0]), "scope" : qUnion([Q1])});
        }
        {
            var Q0;
            Q0=sQuery(id+"F0.wireOp",VERTEX,"E90");
            var Q1;
            Q1=makeQuery(id+"F1.opExtrude","SWEPT_BODY",BODY,{"disambiguationData":[OSD([sQuery(id+"F0.wireOp",EDGE,"E0.left"),sQuery(id+"F0.wireOp",EDGE,"E1.bottom"),sQuery(id+"F0.wireOp",EDGE,"E1.top"),sQuery(id+"F0.wireOp",EDGE,"E1.right")])]});
            hole(context, id + "F18", {"style" : HoleStyle.SIMPLE, "endStyle" : HoleEndStyle.THROUGH, "oppositeDirection" : true, "holeDiameter" : 6.35 * mm, "majorDiameter" : 6.35 * mm, "isTappedThrough" : true, "tappedDepth" : 12.7 * mm, "tapClearance" : 3, "locations" : qUnion([Q0]), "scope" : qUnion([Q1])});
        }
        {
            var Q0;
            Q0=sQuery(id+"F0.wireOp",VERTEX,"E91");
            var Q1;
            Q1=makeQuery(id+"F1.opExtrude","SWEPT_BODY",BODY,{"disambiguationData":[OSD([sQuery(id+"F0.wireOp",EDGE,"E0.left"),sQuery(id+"F0.wireOp",EDGE,"E1.bottom"),sQuery(id+"F0.wireOp",EDGE,"E1.top"),sQuery(id+"F0.wireOp",EDGE,"E1.right")])]});
            hole(context, id + "F19", {"style" : HoleStyle.SIMPLE, "endStyle" : HoleEndStyle.THROUGH, "oppositeDirection" : true, "holeDiameter" : 6.35 * mm, "majorDiameter" : 6.35 * mm, "isTappedThrough" : true, "tappedDepth" : 12.7 * mm, "tapClearance" : 3, "locations" : qUnion([Q0]), "scope" : qUnion([Q1])});
        }
    });
